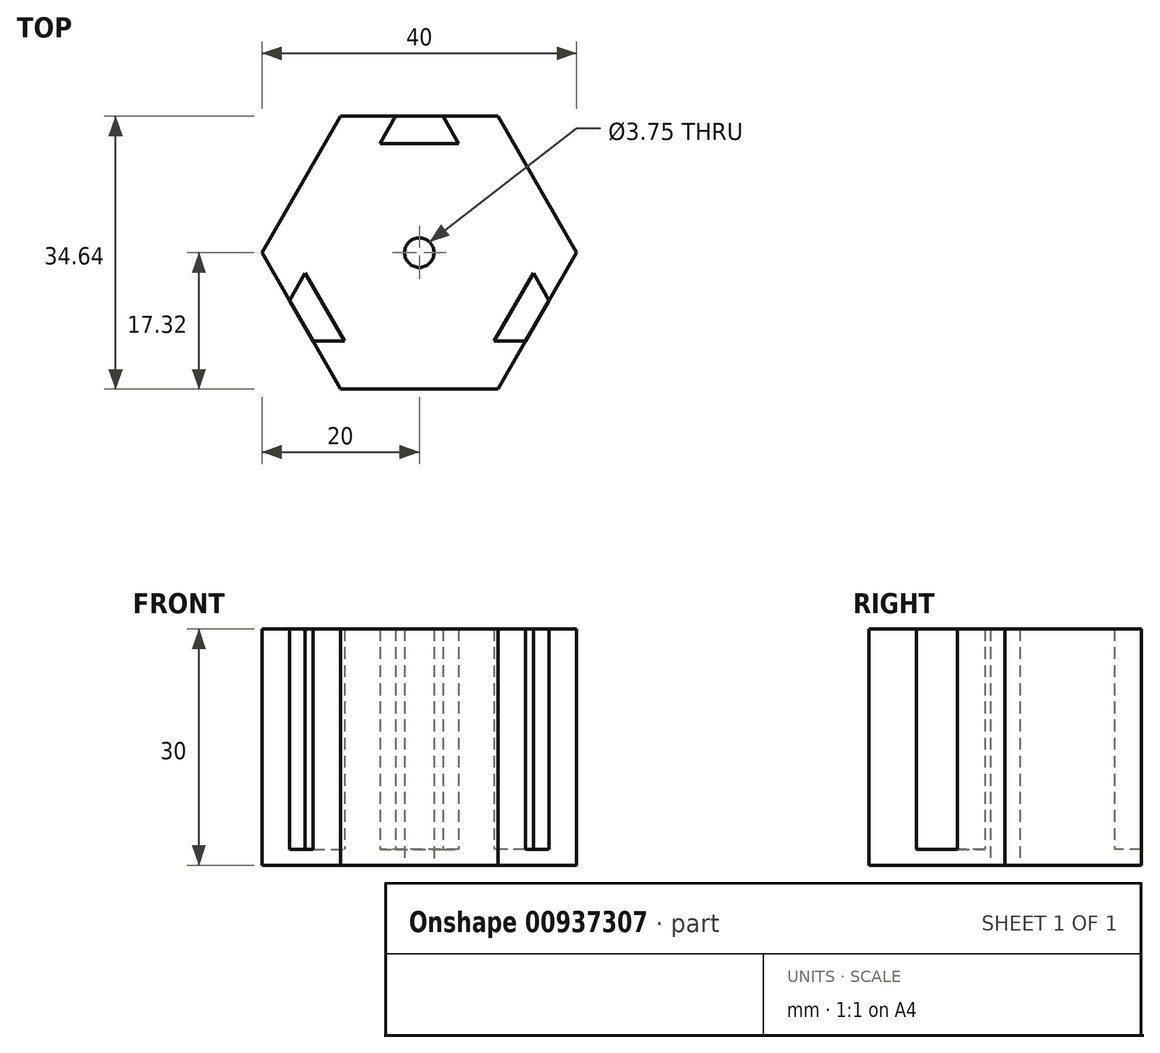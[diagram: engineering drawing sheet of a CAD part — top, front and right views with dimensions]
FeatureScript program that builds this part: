
annotation { "Feature Type Name" : "Feature", "Feature Type Description" : "" }
export const myFeature = defineFeature(function(context is Context, id is Id, definition is map)
    precondition{}
    {
        {
            var Q0;
            Q0=qCreatedBy(makeId("Top.planeOp"),FACE);
            var sketch = newSketch(context, id + "F0", { "sketchPlane" : qUnion([Q0])});
            skCircle(sketch, "E0.cCircle", {"center": v(0, 0) * mm, "radius": 20 * mm, "construction": true});
            skLineSegment(sketch, "E0.0", {"start": v(20, 0) * mm, "end": v(10, -17.32) * mm});
            skLineSegment(sketch, "E0.1", {"start": v(10, -17.32) * mm, "end": v(-10, -17.32) * mm});
            skLineSegment(sketch, "E0.2", {"start": v(-10, -17.32) * mm, "end": v(-20, 0) * mm});
            skLineSegment(sketch, "E0.3", {"start": v(-20, 0) * mm, "end": v(-10, 17.32) * mm});
            skLineSegment(sketch, "E0.4", {"start": v(-10, 17.32) * mm, "end": v(10, 17.32) * mm});
            skLineSegment(sketch, "E0.5", {"start": v(10, 17.32) * mm, "end": v(20, 0) * mm});
            skLineSegment(sketch, "E1", {"start": v(-3, 17.32) * mm, "end": v(3, 17.32) * mm});
            skLineSegment(sketch, "E2", {"start": v(3, 17.32) * mm, "end": v(5, 13.86) * mm});
            skLineSegment(sketch, "E3", {"start": v(5, 13.86) * mm, "end": v(-5, 13.86) * mm});
            skLineSegment(sketch, "E4", {"start": v(-5, 13.86) * mm, "end": v(-3, 17.32) * mm});
            skLineSegment(sketch, "E5.1.0", {"start": v(-14.5, -2.6) * mm, "end": v(-9.5, -11.26) * mm});
            skLineSegment(sketch, "E5.1.1", {"start": v(-9.5, -11.26) * mm, "end": v(-13.5, -11.26) * mm});
            skLineSegment(sketch, "E5.1.2", {"start": v(-16.5, -6.06) * mm, "end": v(-14.5, -2.6) * mm});
            skLineSegment(sketch, "E5.2.0", {"start": v(9.5, -11.26) * mm, "end": v(14.5, -2.6) * mm});
            skLineSegment(sketch, "E5.2.1", {"start": v(14.5, -2.6) * mm, "end": v(16.5, -6.06) * mm});
            skLineSegment(sketch, "E5.2.2", {"start": v(13.5, -11.26) * mm, "end": v(9.5, -11.26) * mm});
            skCircle(sketch, "E6", {"center": v(0, 0) * mm, "radius": 1.88 * mm});
            skSolve(sketch);
        }
        {
            var Q0;
            {var subQ6=sQuery(id+"F0.wireOp",EDGE,"E0.1");Q0=makeQuery(id+"F0.imprint","IMPRINT",FACE,{"disambiguationData":[TD([[makeQuery(id+"F0.imprint","IMPRINT",EDGE,{"derivedFrom":subQ6}),-1.0]])]});}
            extrude(context, id + "F1", {"entities" : qUnion([Q0]), "depth" : 30 * mm, "offsetDistance" : 25 * mm});
        }
        {
            var Q0;
            Q0=makeQuery(id+"F0.imprint","IMPRINT",FACE,{"disambiguationData":[TD([[makeQuery(id+"F0.imprint","IMPRINT",EDGE,{"derivedFrom":sQuery(id+"F0.wireOp",EDGE,"E5.1.0")}),-1.0]])]});
            var Q1;
            Q1=makeQuery(id+"F0.imprint","IMPRINT",FACE,{"disambiguationData":[TD([[makeQuery(id+"F0.imprint","IMPRINT",EDGE,{"derivedFrom":sQuery(id+"F0.wireOp",EDGE,"E5.2.0")}),-1.0]])]});
            var Q2;
            {var subQ0=sQuery(id+"F0.wireOp",EDGE,"E2");Q2=makeQuery(id+"F0.imprint","IMPRINT",FACE,{"disambiguationData":[TD([[makeQuery(id+"F0.imprint","IMPRINT",EDGE,{"derivedFrom":subQ0}),-1.0]])]});}
            extrude(context, id + "F2", {"entities" : qUnion([Q0, Q1, Q2]), "operationType" : NewBodyOperationType.ADD, "depth" : 2 * mm, "offsetDistance" : 25 * mm});
        }
    });
